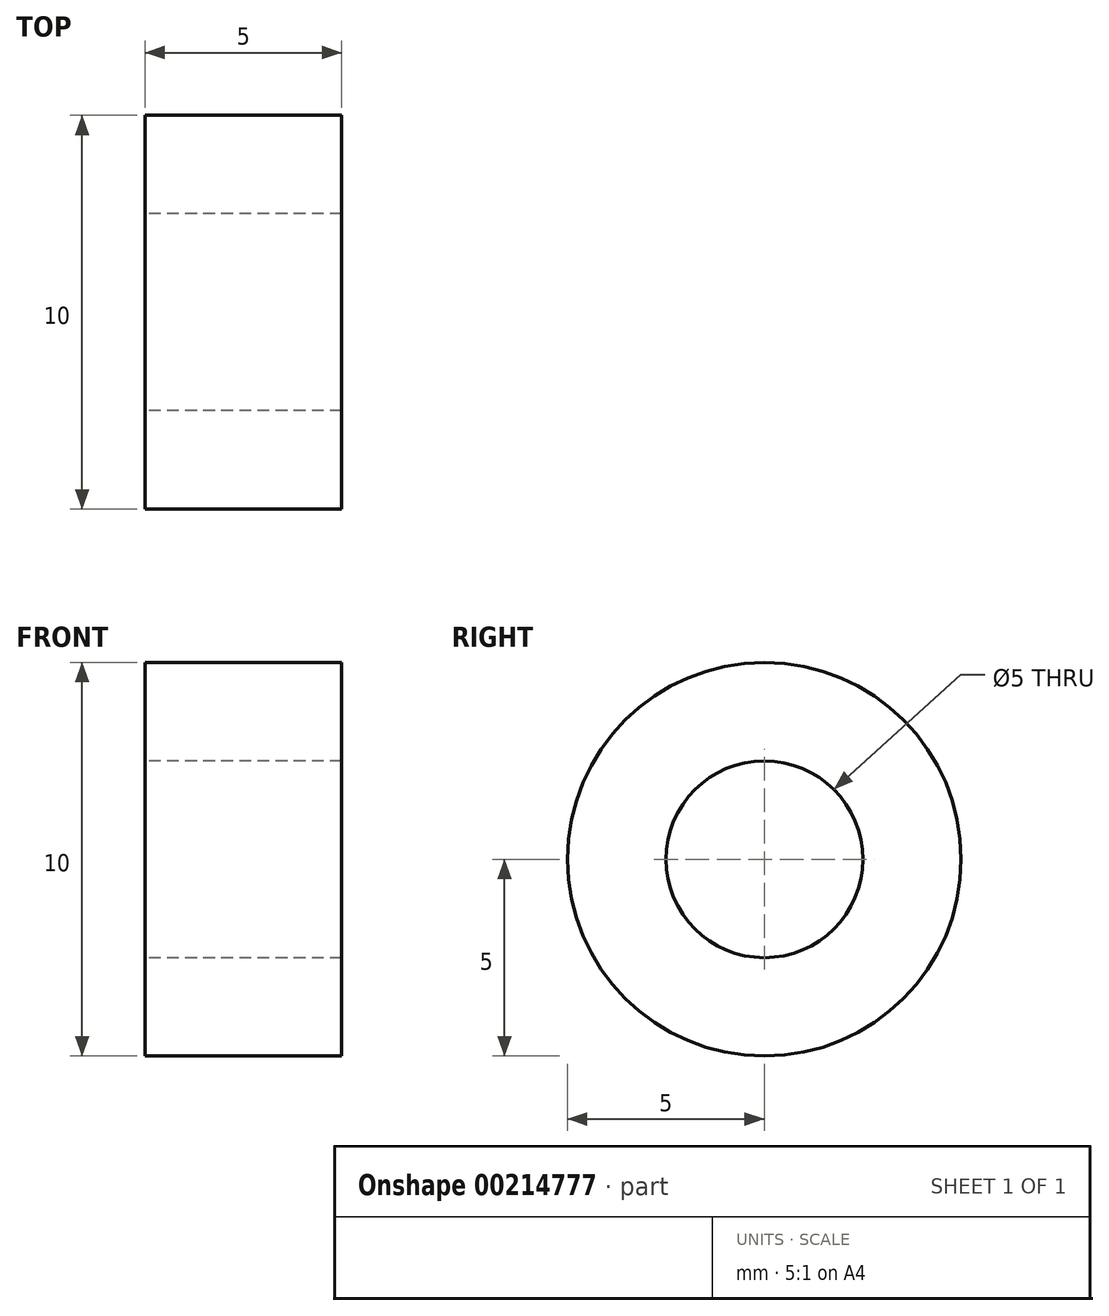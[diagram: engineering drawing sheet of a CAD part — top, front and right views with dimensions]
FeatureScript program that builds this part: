
annotation { "Feature Type Name" : "Feature", "Feature Type Description" : "" }
export const myFeature = defineFeature(function(context is Context, id is Id, definition is map)
    precondition{}
    {
        {
            var Q0;
            Q0=qCreatedBy(makeId("Right.planeOp"),FACE);
            var sketch = newSketch(context, id + "F0", { "sketchPlane" : qUnion([Q0])});
            skCircle(sketch, "E0", {"center": v(0, 0) * mm, "radius": 5 * mm});
            skCircle(sketch, "E1", {"center": v(0, 0) * mm, "radius": 2.5 * mm});
            skSolve(sketch);
        }
        {
            var Q0;
            Q0=makeQuery(id+"F0.imprint","IMPRINT",FACE,{"disambiguationData":[TD([[makeQuery(id+"F0.imprint","IMPRINT",EDGE,{"derivedFrom":sQuery(id+"F0.wireOp",EDGE,"E0")}),1.0]])]});
            extrude(context, id + "F1", {"entities" : qUnion([Q0]), "depth" : 5 * mm});
        }
    });
